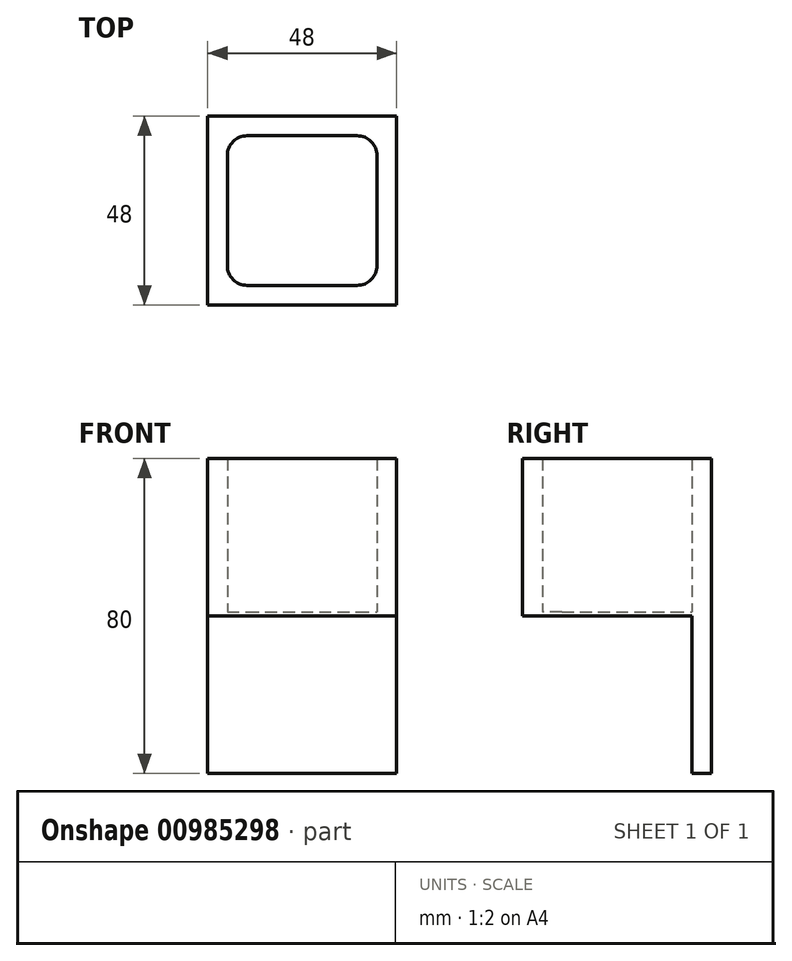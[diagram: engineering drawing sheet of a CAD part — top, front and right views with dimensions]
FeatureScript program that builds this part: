
annotation { "Feature Type Name" : "Feature", "Feature Type Description" : "" }
export const myFeature = defineFeature(function(context is Context, id is Id, definition is map)
    precondition{}
    {
        {
            var Q0;
            Q0=qCreatedBy(makeId("Top.planeOp"),FACE);
            var sketch = newSketch(context, id + "F0", { "sketchPlane" : qUnion([Q0])});
            skLineSegment(sketch, "E0.bottom", {"start": v(0, 0) * mm, "end": v(38, 0) * mm});
            skLineSegment(sketch, "E0.top", {"start": v(0, 38) * mm, "end": v(38, 38) * mm});
            skLineSegment(sketch, "E0.left", {"start": v(0, 0) * mm, "end": v(0, 38) * mm});
            skLineSegment(sketch, "E0.right", {"start": v(38, 0) * mm, "end": v(38, 38) * mm});
            skLineSegment(sketch, "E1.0", {"start": v(-5, 43) * mm, "end": v(43, 43) * mm});
            skLineSegment(sketch, "E1.1", {"start": v(-5, -5) * mm, "end": v(-5, 43) * mm});
            skLineSegment(sketch, "E1.2", {"start": v(-5, -5) * mm, "end": v(43, -5) * mm});
            skLineSegment(sketch, "E1.3", {"start": v(43, -5) * mm, "end": v(43, 43) * mm});
            skLineSegment(sketch, "E2", {"start": v(38, 38) * mm, "end": v(43, 38) * mm});
            skLineSegment(sketch, "E3", {"start": v(43, 38) * mm, "end": v(0, 38) * mm});
            skLineSegment(sketch, "E4", {"start": v(0, 38) * mm, "end": v(-5, 38) * mm});
            skSolve(sketch);
        }
        {
            var Q0;
            Q0=makeQuery(id+"F0.imprint","IMPRINT",FACE,{"disambiguationData":[TD([[makeQuery(id+"F0.imprint","IMPRINT",EDGE,{"derivedFrom":sQuery(id+"F0.wireOp",EDGE,"E0.bottom")}),1.0]])]});
            extrude(context, id + "F1", {"entities" : qUnion([Q0]), "depth" : 1 * mm, "offsetDistance" : 25 * mm});
        }
        {
            var Q0;
            Q0=makeQuery(id+"F0.imprint","IMPRINT",FACE,{"disambiguationData":[TD([[makeQuery(id+"F0.imprint","IMPRINT",EDGE,{"derivedFrom":sQuery(id+"F0.wireOp",EDGE,"E0.bottom")}),-1.0]])]});
            var Q1;
            Q1=makeQuery(id+"F0.imprint","IMPRINT",FACE,{"disambiguationData":[TD([[makeQuery(id+"F0.imprint","IMPRINT",EDGE,{"derivedFrom":sQuery(id+"F0.wireOp",EDGE,"E0.top")}),1.0]])]});
            extrude(context, id + "F2", {"entities" : qUnion([Q0, Q1]), "operationType" : NewBodyOperationType.ADD, "depth" : 40 * mm, "offsetDistance" : 25 * mm});
        }
        {
            var Q0;
            Q0=makeQuery(id+"F0.imprint","IMPRINT",FACE,{"disambiguationData":[TD([[makeQuery(id+"F0.imprint","IMPRINT",EDGE,{"derivedFrom":sQuery(id+"F0.wireOp",EDGE,"E0.top")}),1.0]])]});
            extrude(context, id + "F3", {"entities" : qUnion([Q0]), "operationType" : NewBodyOperationType.ADD, "oppositeDirection" : true, "depth" : 40 * mm, "offsetDistance" : 25 * mm});
        }
        {
            var Q0;
            Q0=makeQuery(id+"F2.opExtrude","SWEPT_EDGE",EDGE,{"disambiguationData":[OSD([sQuery(id+"F0.wireOp",EDGE,"E0.top"),sQuery(id+"F0.wireOp",EDGE,"E0.left"),sQuery(id+"F0.wireOp",EDGE,"E4")])]});
            var Q1;
            Q1=makeQuery(id+"F2.opExtrude","SWEPT_EDGE",EDGE,{"disambiguationData":[OSD([sQuery(id+"F0.wireOp",EDGE,"E0.top"),sQuery(id+"F0.wireOp",EDGE,"E0.right"),sQuery(id+"F0.wireOp",EDGE,"E2")])]});
            var Q2;
            Q2=makeQuery(id+"F2.opExtrude","SWEPT_EDGE",EDGE,{"disambiguationData":[OSD([sQuery(id+"F0.wireOp",EDGE,"E0.bottom"),sQuery(id+"F0.wireOp",EDGE,"E0.right")])]});
            var Q3;
            Q3=makeQuery(id+"F2.opExtrude","SWEPT_EDGE",EDGE,{"disambiguationData":[OSD([sQuery(id+"F0.wireOp",EDGE,"E0.bottom"),sQuery(id+"F0.wireOp",EDGE,"E0.left")])]});
            fillet(context, id + "F4", {"entities" : qUnion([Q0, Q1, Q2, Q3]), "radius" : 5 * mm, "tangentPropagation" : true, "allowEdgeOverflow" : false});
        }
    });
